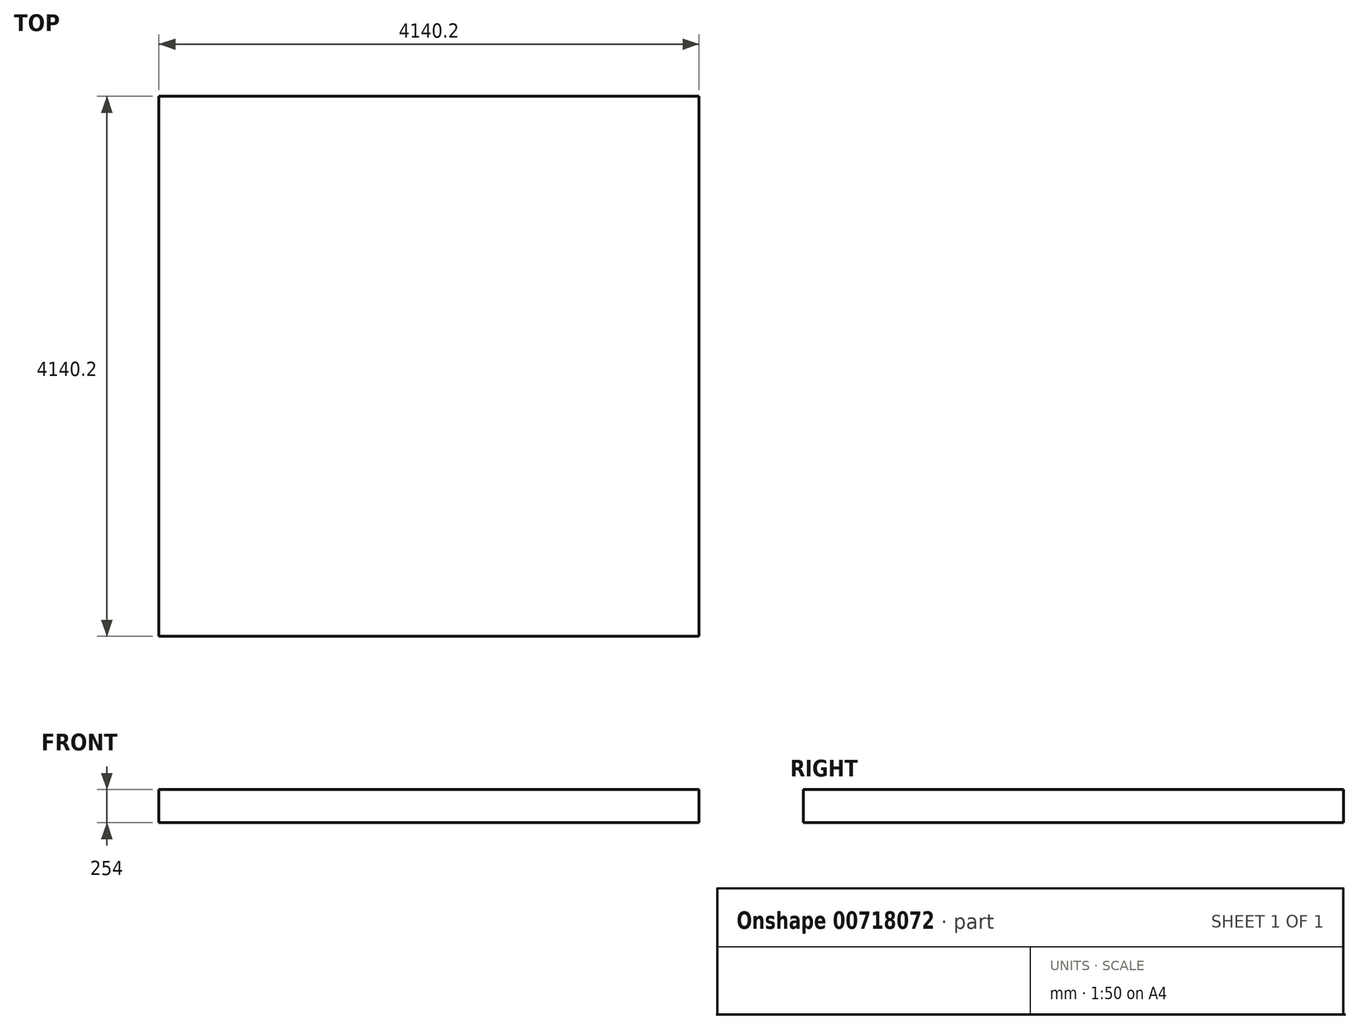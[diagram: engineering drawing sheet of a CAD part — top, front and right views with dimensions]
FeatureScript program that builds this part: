
annotation { "Feature Type Name" : "Feature", "Feature Type Description" : "" }
export const myFeature = defineFeature(function(context is Context, id is Id, definition is map)
    precondition{}
    {
        {
            var Q0;
            Q0=qCreatedBy(makeId("Top.planeOp"),FACE);
            var sketch = newSketch(context, id + "F0", { "sketchPlane" : qUnion([Q0])});
            skLineSegment(sketch, "E0.bottom", {"start": v(2070.1, -2070.1) * mm, "end": v(-2070.1, -2070.1) * mm});
            skLineSegment(sketch, "E0.top", {"start": v(2070.1, 2070.1) * mm, "end": v(-2070.1, 2070.1) * mm});
            skLineSegment(sketch, "E0.left", {"start": v(2070.1, -2070.1) * mm, "end": v(2070.1, 2070.1) * mm});
            skLineSegment(sketch, "E0.right", {"start": v(-2070.1, -2070.1) * mm, "end": v(-2070.1, 2070.1) * mm});
            skPoint(sketch, "E0.middle", {"position": v(0, 0) * mm});
            skSolve(sketch);
        }
        {
            var Q0;
            Q0 = qSketchRegion(id + "F0", true);
            extrude(context, id + "F1", {"entities" : qUnion([Q0]), "depth" : 254 * mm, "offsetDistance" : 25.4 * mm});
        }
    });
